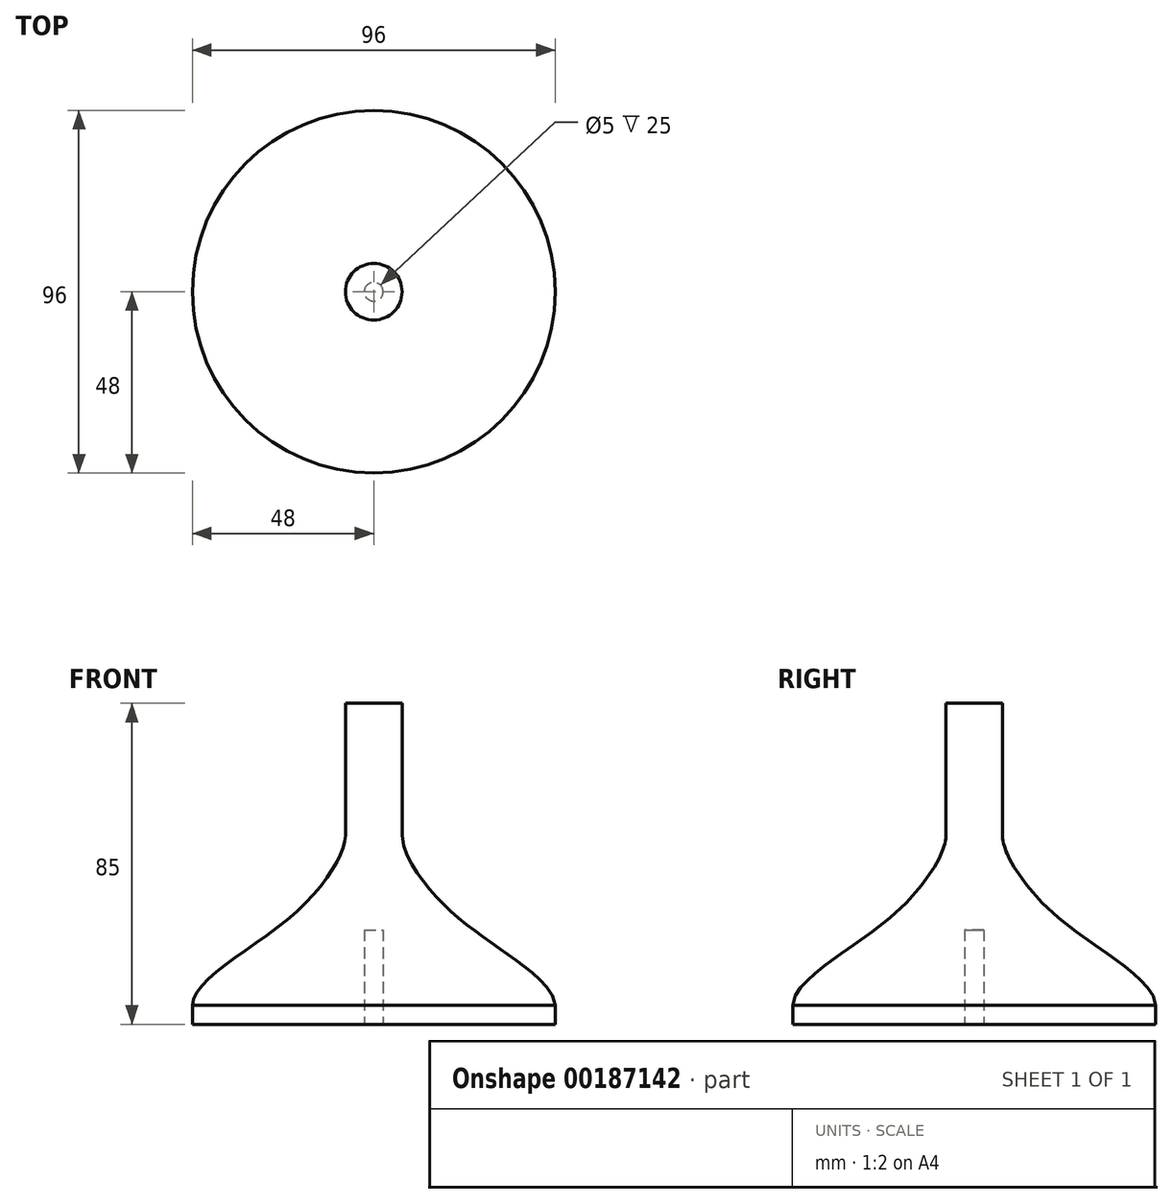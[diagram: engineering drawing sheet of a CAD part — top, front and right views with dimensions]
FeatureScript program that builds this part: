
annotation { "Feature Type Name" : "Feature", "Feature Type Description" : "" }
export const myFeature = defineFeature(function(context is Context, id is Id, definition is map)
    precondition{}
    {
        {
            var Q0;
            Q0=qCreatedBy(makeId("Front.planeOp"),FACE);
            var sketch = newSketch(context, id + "F0", { "sketchPlane" : qUnion([Q0])});
            skLineSegment(sketch, "E0", {"start": v(0, 0) * mm, "end": v(48, 0) * mm});
            skLineSegment(sketch, "E1", {"start": v(0, 0) * mm, "end": v(0, 85) * mm});
            skLineSegment(sketch, "E2", {"start": v(0, 85) * mm, "end": v(7.5, 85) * mm});
            skLineSegment(sketch, "E3", {"start": v(7.5, 85) * mm, "end": v(7.5, 50) * mm});
            skLineSegment(sketch, "E4", {"start": v(48, 0) * mm, "end": v(48, 5) * mm});
            skFitSpline(sketch, "E5", {"points": [v(48, 5) * mm, v(22.1, 28.4) * mm, v(7.5, 50) * mm], "startDerivative": vector(-1.29, 40) * mm, "endDerivative": vector(-0.28, 32.4) * mm});
            skSolve(sketch);
        }
        {
            var Q0;
            Q0=makeQuery(id+"F0.imprint","IMPRINT",FACE,{"disambiguationData":[TD([[makeQuery(id+"F0.imprint","IMPRINT",EDGE,{"derivedFrom":sQuery(id+"F0.wireOp",EDGE,"E0")}),1.0]])]});
            var Q1;
            Q1=sQuery(id+"F0.wireOp",EDGE,"E1");
            revolve(context, id + "F1", {"entities" : qUnion([Q0]), "axis" : qUnion([Q1]), "revolveType" : RevolveType.FULL});
        }
        {
            var Q0;
            Q0=makeQuery(id+"F1.opRevolve","SWEPT_FACE",FACE,{"disambiguationData":[OSD([sQuery(id+"F0.wireOp",EDGE,"E0")])]});
            var sketch = newSketch(context, id + "F2", { "sketchPlane" : qUnion([Q0])});
            skCircle(sketch, "E6", {"center": v(0, 0) * mm, "radius": 2.5 * mm});
            skSolve(sketch);
        }
        {
            var Q0;
            Q0 = qSketchRegion(id + "F2", true);
            extrude(context, id + "F3", {"entities" : qUnion([Q0]), "operationType" : NewBodyOperationType.REMOVE, "oppositeDirection" : true, "depth" : 25 * mm});
        }
    });
